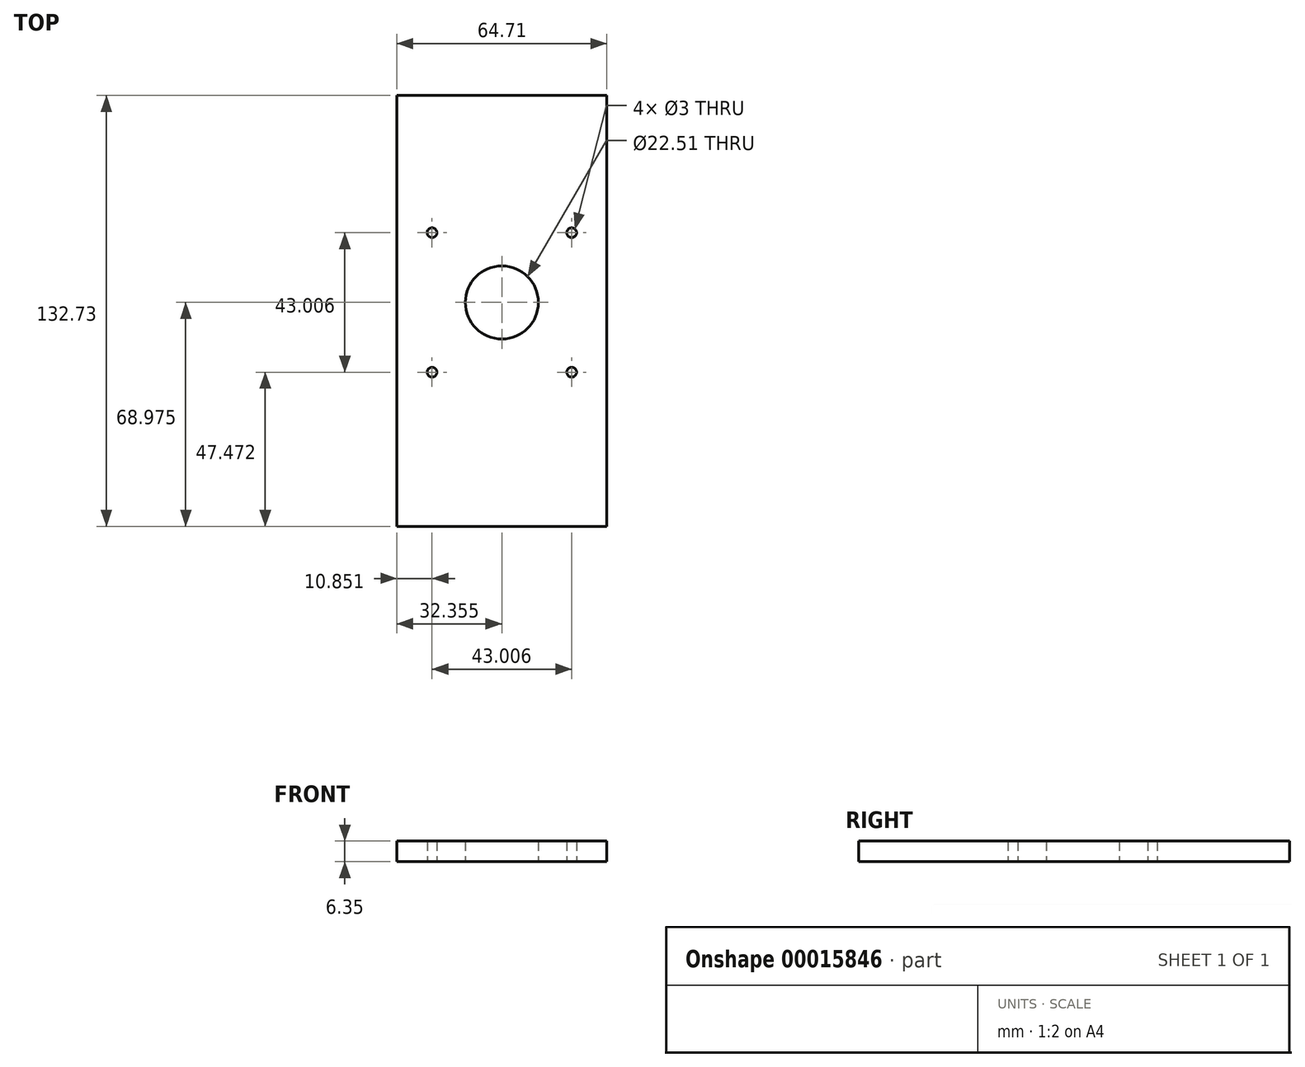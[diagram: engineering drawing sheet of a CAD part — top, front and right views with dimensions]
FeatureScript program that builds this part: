
annotation { "Feature Type Name" : "Feature", "Feature Type Description" : "" }
export const myFeature = defineFeature(function(context is Context, id is Id, definition is map)
    precondition{}
    {
        {
            var Q0;
            Q0=qCreatedBy(makeId("Top.planeOp"),FACE);
            var sketch = newSketch(context, id + "F0", { "sketchPlane" : qUnion([Q0])});
            skLineSegment(sketch, "E0.bottom", {"start": v(0, 0) * mm, "end": v(64.7, 0) * mm});
            skLineSegment(sketch, "E0.top", {"start": v(0, -132.73) * mm, "end": v(64.7, -132.73) * mm});
            skLineSegment(sketch, "E0.left", {"start": v(0, 0) * mm, "end": v(0, -132.73) * mm});
            skLineSegment(sketch, "E0.right", {"start": v(64.7, 0) * mm, "end": v(64.7, -132.73) * mm});
            skLineSegment(sketch, "E1.rect.bottom", {"start": v(53.86, -42.25) * mm, "end": v(10.85, -42.25) * mm, "construction": true});
            skLineSegment(sketch, "E1.rect.top", {"start": v(53.86, -85.26) * mm, "end": v(10.85, -85.26) * mm, "construction": true});
            skLineSegment(sketch, "E1.rect.left", {"start": v(53.86, -42.25) * mm, "end": v(53.86, -85.26) * mm, "construction": true});
            skLineSegment(sketch, "E1.rect.right", {"start": v(10.85, -42.25) * mm, "end": v(10.85, -85.26) * mm, "construction": true});
            skPoint(sketch, "E1.rect.middle", {"position": v(32.35, -63.75) * mm});
            skCircle(sketch, "E2", {"center": v(32.35, -63.75) * mm, "radius": 11.25 * mm});
            skCircle(sketch, "E3", {"center": v(53.86, -42.25) * mm, "radius": 1.5 * mm});
            skCircle(sketch, "E4", {"center": v(10.85, -42.25) * mm, "radius": 1.5 * mm});
            skCircle(sketch, "E5", {"center": v(10.85, -85.26) * mm, "radius": 1.5 * mm});
            skCircle(sketch, "E6", {"center": v(53.86, -85.26) * mm, "radius": 1.5 * mm});
            skLineSegment(sketch, "E7", {"start": v(32.35, -63.75) * mm, "end": v(32.35, 0) * mm});
            skSolve(sketch);
        }
        {
            var Q0;
            Q0 = qSketchRegion(id + "F0", true);
            extrude(context, id + "F1", {"entities" : qUnion([Q0]), "depth" : 6.35 * mm});
        }
    });
